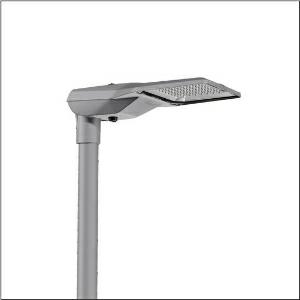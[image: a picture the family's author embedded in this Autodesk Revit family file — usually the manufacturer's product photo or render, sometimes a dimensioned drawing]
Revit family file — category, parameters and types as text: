
# Revit family: streetlight_sl_21_midi___st1_0a_5xe3d43t08lb_efa2
name_source: partatom
category: Lighting Fixtures
units: mm (PartAtom-declared; Revit-internal decimal feet)

## family parameters
Cut with Voids When Loaded = No
Host = Face
Light Source = No
Part Type = Normal
Room Calculation Point = No
Round Connector Dimension = Use Diameter
Shared = No

## types (1)
- --- (1 x LED, 14950 lm, 99.6 W, 4000K)
    Apparent Load = 100 VA
    CIE Flux Codes = 37 72 97 100 100
    Color Rendering = 70
    Color Temperature = 4000K
    Default Elevation = 1800 mm
    Description = Streetlight SL 21 midi, mast luminaire, primary light control with lens, of PMMA, primary optical cover: cover, of toughened safety glass, transparent, light distribution: ST1.0a, light emission: direct distribution, primary light characteristic: asymmetric, installation type: side-entry, post-top, LED, High Power LED, rated luminous flux: 14.950lm, luminous efficacy: 150lm/W, light colour: 740, colour temperature: 4000K, control gear: D4i, control: overheat protection, constant luminous flux control, time-dependent luminous flux control, flexible luminous flux parameterisation, pre-setting: logarithmic dimming characteristic, mains connection: 230..240V, AC, 50/60Hz, start of lifetime: 100W, end of service life: 102W, reduction: 46W, luminaire housing, of diecast aluminium, powder-coated, Siteco® metallic grey (DB 702S), corrosivity category C5 mid according to DIN EN ISO 12944, please order mast flange separately, inclination adjustable: 0°, 5°, 10°, 15°, sealing non-destructively replaceable, multi-level sealing system, length: 644mm, width: 335mm, height: 110mm, mast flange for spigot size: 42mm (side-entry): 5XC10008XM4, 60/48mm (side-entry/post-top): 5XC10108XM2, 76/60mm (side-entry/post-top): 5XC10108XM1, mounting height: 4..8m, Smart Interface below and above, protection rating (complete): IP66, insulation class (complete): insulation class II (safety insulation), certification: CE, ENEC, ENEC+, VDE, impact resistance: IK10, permissible operating ambient temperature for outdoor applications: -40..+50°C, standard-compliant lighting for roads and squares, packaging unit: 1 piece

Light Distribution: ST1.0a
    Height = 111 mm
    Lamp = 1 x LED
    Lamp Light Flux = 14950 lm
    Lamp Power = 99.6 W
    Lamp count = 1
    Length = 644 mm
    Luminous efficacy = 150 lm/W
    Manufacturer = Siteco
    ModVariant = No
    Model = 5XE3D43T08LB
    Number of Poles = 1
    OnlyDefault = Yes
    Power Factor = 1
    Product Name = Streetlight SL 21 midi | ST1.0a
    Product group = mast luminaire | pylon top
    ProductGroupID = 6100
    Protection Class = Protection class II
    Protection Degree = IP 66
    RLX_Detail_Level = 1
    RLX_Emergency_Light_Flux = 0 lm
    RLX_Emergency_Type = 0
    RLX_Emergency_Type_DB = No
    RlxData = <blob elided: 26853 chars, md5=26213d0d>
    Socket = socket
    Standby Power = 0 W
    System Light Flux = 14950 lm
    System Power = 100 W
    Type Comments = factory setting: luminous flux: 100 % | dim-lin: 254 | 1020 mA
    Type Image = l_1004304.jpg
    URL = http://relux.com
    VarID = @adj_032009
    Voltage = 0 V
    Weight = 0.00 kg
    Width = 336 mm

## geometry (parser evidence)
native form markers: Blend x4, Sweep x13
no freeform markers — native parametric forms only
